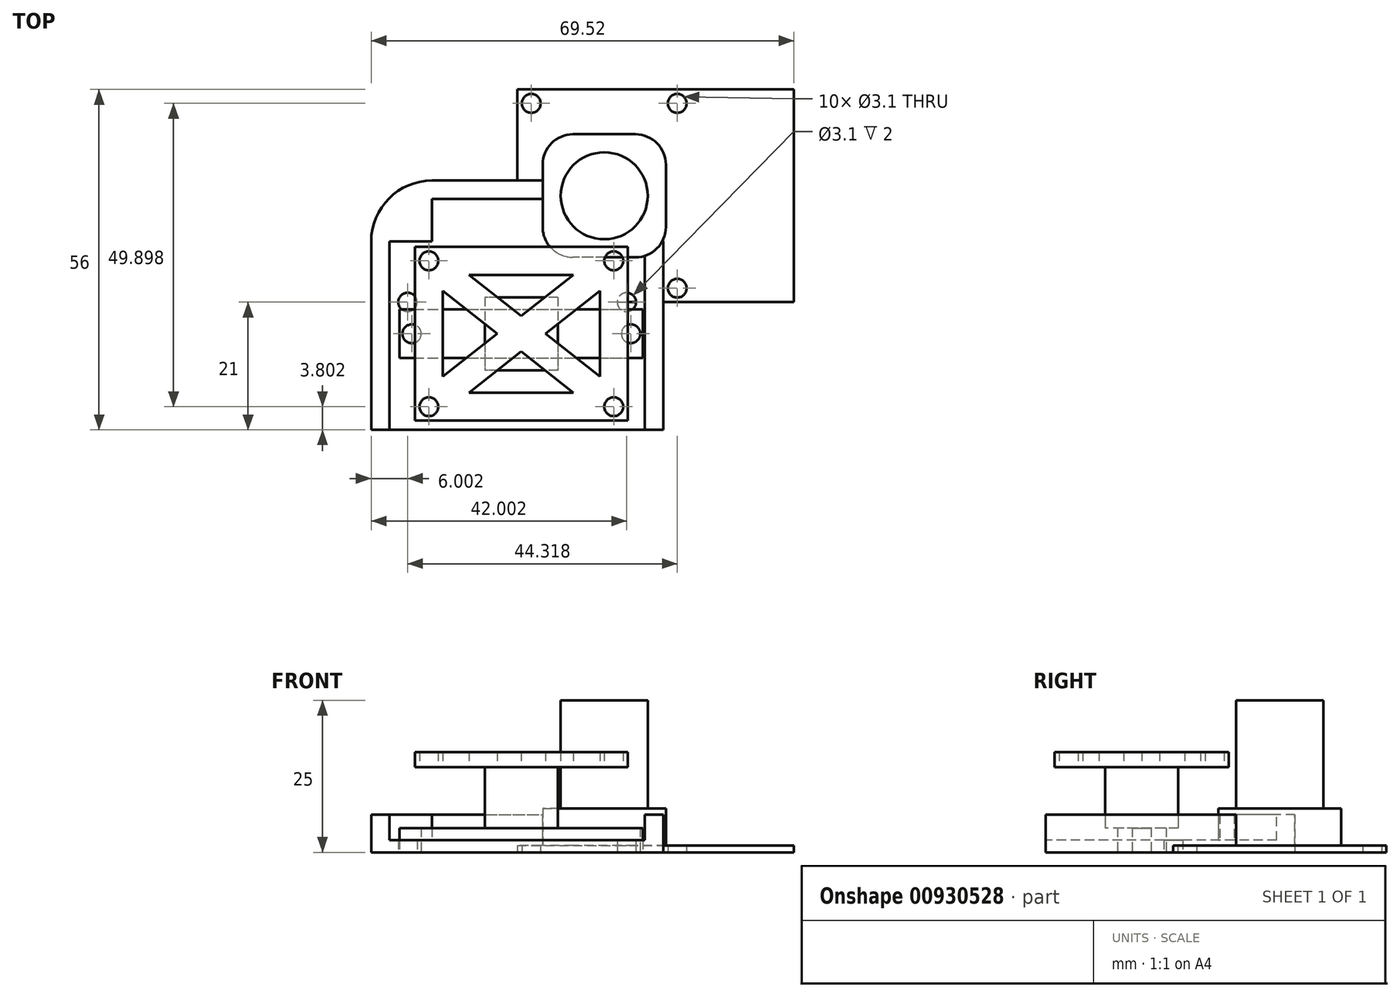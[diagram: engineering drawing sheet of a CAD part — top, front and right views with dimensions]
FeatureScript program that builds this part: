
annotation { "Feature Type Name" : "Feature", "Feature Type Description" : "" }
export const myFeature = defineFeature(function(context is Context, id is Id, definition is map)
    precondition{}
    {
        {
            var Q0;
            Q0=qCreatedBy(makeId("Top.planeOp"),FACE);
            var sketch = newSketch(context, id + "F0", { "sketchPlane" : qUnion([Q0])});
            skLineSegment(sketch, "E0.bottom", {"start": v(0, 0) * mm, "end": v(45.5, 0) * mm});
            skLineSegment(sketch, "E0.top", {"start": v(0, 35) * mm, "end": v(45.5, 35) * mm});
            skLineSegment(sketch, "E0.left", {"start": v(0, 0) * mm, "end": v(0, 35) * mm});
            skLineSegment(sketch, "E0.right", {"start": v(45.5, 0) * mm, "end": v(45.5, 35) * mm});
            skPoint(sketch, "E1", {"position": v(2.3, 32.7) * mm});
            skPoint(sketch, "E2", {"position": v(2.3, 2.3) * mm});
            skPoint(sketch, "E3", {"position": v(26.3, 2.3) * mm});
            skPoint(sketch, "E4", {"position": v(26.3, 32.7) * mm});
            skCircle(sketch, "E5", {"center": v(2.3, 32.7) * mm, "radius": 1.55 * mm});
            skCircle(sketch, "E6", {"center": v(26.3, 32.7) * mm, "radius": 1.55 * mm});
            skCircle(sketch, "E7", {"center": v(26.3, 2.3) * mm, "radius": 1.55 * mm});
            skCircle(sketch, "E8", {"center": v(2.3, 2.3) * mm, "radius": 1.55 * mm});
            skPoint(sketch, "E9", {"position": v(0, 17.5) * mm});
            skPoint(sketch, "E10", {"position": v(22.75, 35) * mm});
            skPoint(sketch, "E11", {"position": v(14.3, 17.5) * mm});
            skLineSegment(sketch, "E12", {"start": v(2.3, 32.7) * mm, "end": v(26.3, 32.7) * mm, "construction": true});
            skLineSegment(sketch, "E13", {"start": v(2.3, 32.7) * mm, "end": v(2.3, 2.3) * mm, "construction": true});
            skPoint(sketch, "E14", {"position": v(14.3, 32.7) * mm});
            skPoint(sketch, "E15", {"position": v(2.3, 17.5) * mm});
            skLineSegment(sketch, "E16.bottom", {"start": v(19.42, 27.63) * mm, "end": v(9.17, 27.63) * mm});
            skLineSegment(sketch, "E16.top", {"start": v(19.42, 7.38) * mm, "end": v(9.18, 7.38) * mm});
            skLineSegment(sketch, "E16.left", {"start": v(24.43, 22.62) * mm, "end": v(24.43, 12.38) * mm});
            skLineSegment(sketch, "E16.right", {"start": v(4.17, 22.62) * mm, "end": v(4.17, 12.38) * mm});
            skPoint(sketch, "E17.visualSharp", {"position": v(4.17, 27.63) * mm});
            skArc(sketch, "E17.filletArc", {"start": v(9.17, 27.63) * mm, "mid": v(5.64, 26.16) * mm, "end": v(4.17, 22.62) * mm});
            skPoint(sketch, "E18.visualSharp", {"position": v(4.18, 7.38) * mm});
            skArc(sketch, "E18.filletArc", {"start": v(4.17, 12.38) * mm, "mid": v(5.64, 8.84) * mm, "end": v(9.18, 7.38) * mm});
            skPoint(sketch, "E19.visualSharp", {"position": v(24.42, 27.63) * mm});
            skArc(sketch, "E19.filletArc", {"start": v(24.43, 22.62) * mm, "mid": v(22.96, 26.16) * mm, "end": v(19.42, 27.63) * mm});
            skPoint(sketch, "E20.visualSharp", {"position": v(24.43, 7.38) * mm});
            skArc(sketch, "E20.filletArc", {"start": v(19.42, 7.38) * mm, "mid": v(22.96, 8.84) * mm, "end": v(24.42, 12.38) * mm});
            skCircle(sketch, "E21", {"center": v(14.3, 17.5) * mm, "radius": 7.15 * mm});
            skSolve(sketch);
        }
        {
            var Q0;
            Q0=makeQuery(id+"F0.imprint","IMPRINT",FACE,{"disambiguationData":[TD([[makeQuery(id+"F0.imprint","IMPRINT",EDGE,{"derivedFrom":sQuery(id+"F0.wireOp",EDGE,"E0.bottom")}),1.0]])]});
            extrude(context, id + "F1", {"entities" : qUnion([Q0]), "depth" : 1.1 * mm, "offsetDistance" : 25 * mm});
        }
        {
            var Q0;
            Q0=makeQuery(id+"F0.imprint","IMPRINT",FACE,{"disambiguationData":[TD([[makeQuery(id+"F0.imprint","IMPRINT",EDGE,{"derivedFrom":sQuery(id+"F0.wireOp",EDGE,"E16.bottom")}),1.0]])]});
            extrude(context, id + "F2", {"entities" : qUnion([Q0]), "operationType" : NewBodyOperationType.ADD, "depth" : 7.2 * mm, "offsetDistance" : 25 * mm});
        }
        {
            var Q0;
            Q0=makeQuery(id+"F0.imprint","IMPRINT",FACE,{"disambiguationData":[TD([[makeQuery(id+"F0.imprint","IMPRINT",EDGE,{"derivedFrom":sQuery(id+"F0.wireOp",EDGE,"E21")}),1.0]])]});
            extrude(context, id + "F3", {"entities" : qUnion([Q0]), "operationType" : NewBodyOperationType.ADD, "depth" : 25 * mm, "offsetDistance" : 25 * mm});
        }
        {
            var Q0;
            Q0=qCreatedBy(makeId("Top.planeOp"),FACE);
            var sketch = newSketch(context, id + "F4", { "sketchPlane" : qUnion([Q0])});
            skLineSegment(sketch, "E22.bottom", {"start": v(-14.02, 20) * mm, "end": v(13.98, 20) * mm});
            skLineSegment(sketch, "E22.top", {"start": v(-24.02, -21) * mm, "end": v(23.98, -21) * mm});
            skLineSegment(sketch, "E22.left", {"start": v(-24.02, 10) * mm, "end": v(-24.02, -21) * mm});
            skLineSegment(sketch, "E22.right", {"start": v(23.98, 10) * mm, "end": v(23.98, -21) * mm});
            skPoint(sketch, "E23.visualSharp", {"position": v(-24.02, 20) * mm});
            skArc(sketch, "E23.filletArc", {"start": v(-14.02, 20) * mm, "mid": v(-21.09, 17.07) * mm, "end": v(-24.02, 10) * mm});
            skPoint(sketch, "E24.visualSharp", {"position": v(23.98, 20) * mm});
            skArc(sketch, "E24.filletArc", {"start": v(23.98, 10) * mm, "mid": v(21.05, 17.07) * mm, "end": v(13.98, 20) * mm});
            skLineSegment(sketch, "E25.0", {"start": v(-21.02, 10) * mm, "end": v(-21.02, -21) * mm});
            skLineSegment(sketch, "E25.1", {"start": v(20.98, 10) * mm, "end": v(20.98, -21) * mm});
            skArc(sketch, "E25.2", {"start": v(20.98, 10) * mm, "mid": v(18.93, 14.95) * mm, "end": v(13.98, 17) * mm});
            skLineSegment(sketch, "E25.3", {"start": v(-14.02, 17) * mm, "end": v(13.98, 17) * mm});
            skArc(sketch, "E25.4", {"start": v(-14.02, 17) * mm, "mid": v(-18.97, 14.95) * mm, "end": v(-21.02, 10) * mm});
            skPoint(sketch, "E26", {"position": v(17.98, 0) * mm});
            skPoint(sketch, "E27", {"position": v(-18.02, 0) * mm});
            skCircle(sketch, "E28", {"center": v(-18.02, 0) * mm, "radius": 1.55 * mm});
            skCircle(sketch, "E29", {"center": v(17.98, 0) * mm, "radius": 1.55 * mm});
            skLineSegment(sketch, "E30", {"start": v(-21.02, 10) * mm, "end": v(-14.02, 10) * mm});
            skLineSegment(sketch, "E31", {"start": v(-14.02, 17) * mm, "end": v(-14.02, 10) * mm});
            skLineSegment(sketch, "E32", {"start": v(13.98, 17) * mm, "end": v(13.98, 10) * mm});
            skLineSegment(sketch, "E33", {"start": v(20.98, 10) * mm, "end": v(13.98, 10) * mm});
            skSolve(sketch);
        }
        {
            var Q0;
            {var subQ1=sQuery(id+"F4.wireOp",EDGE,"E25.0");Q0=makeQuery(id+"F4.imprint","IMPRINT",FACE,{"disambiguationData":[TD([[makeQuery(id+"F4.imprint","IMPRINT",EDGE,{"derivedFrom":subQ1}),1.0]])]});}
            extrude(context, id + "F5", {"entities" : qUnion([Q0]), "depth" : 2 * mm, "offsetDistance" : 25 * mm});
        }
        {
            var Q0;
            Q0=makeQuery(id+"F4.imprint","IMPRINT",FACE,{"disambiguationData":[TD([[makeQuery(id+"F4.imprint","IMPRINT",EDGE,{"derivedFrom":sQuery(id+"F4.wireOp",EDGE,"E22.bottom")}),-1.0]])]});
            var Q1;
            Q1=makeQuery(id+"F4.imprint","IMPRINT",FACE,{"disambiguationData":[TD([[makeQuery(id+"F4.imprint","IMPRINT",EDGE,{"derivedFrom":sQuery(id+"F4.wireOp",EDGE,"E25.2")}),1.0]])]});
            var Q2;
            Q2=makeQuery(id+"F4.imprint","IMPRINT",FACE,{"disambiguationData":[TD([[makeQuery(id+"F4.imprint","IMPRINT",EDGE,{"derivedFrom":sQuery(id+"F4.wireOp",EDGE,"E25.4")}),1.0]])]});
            extrude(context, id + "F6", {"entities" : qUnion([Q0, Q1, Q2]), "operationType" : NewBodyOperationType.ADD, "depth" : 6.17 * mm, "offsetDistance" : 25 * mm});
        }
        {
            var Q0;
            Q0=qCreatedBy(makeId("Top.planeOp"),FACE);
            var sketch = newSketch(context, id + "F7", { "sketchPlane" : qUnion([Q0])});
            skLineSegment(sketch, "E34.bottom", {"start": v(-19.33, -1.2) * mm, "end": v(20.67, -1.2) * mm});
            skLineSegment(sketch, "E34.top", {"start": v(-19.33, -9.2) * mm, "end": v(20.67, -9.2) * mm});
            skLineSegment(sketch, "E34.left", {"start": v(-19.33, -1.2) * mm, "end": v(-19.33, -9.2) * mm});
            skLineSegment(sketch, "E34.right", {"start": v(20.67, -1.2) * mm, "end": v(20.67, -9.2) * mm});
            skPoint(sketch, "E35", {"position": v(0.67, -1.2) * mm});
            skPoint(sketch, "E36", {"position": v(-19.33, -5.2) * mm});
            skPoint(sketch, "E37", {"position": v(-17.33, -5.2) * mm});
            skPoint(sketch, "E38", {"position": v(18.67, -5.2) * mm});
            skCircle(sketch, "E39", {"center": v(-17.33, -5.2) * mm, "radius": 1.55 * mm});
            skCircle(sketch, "E40", {"center": v(18.67, -5.2) * mm, "radius": 1.55 * mm});
            skSolve(sketch);
        }
        {
            var Q0;
            Q0=makeQuery(id+"F7.imprint","IMPRINT",FACE,{"disambiguationData":[TD([[makeQuery(id+"F7.imprint","IMPRINT",EDGE,{"derivedFrom":sQuery(id+"F7.wireOp",EDGE,"E34.bottom")}),-1.0]])]});
            extrude(context, id + "F8", {"entities" : qUnion([Q0]), "depth" : 4 * mm, "offsetDistance" : 25 * mm});
        }
        {
            var Q0;
            Q0=makeQuery(id+"F8.opExtrude","CAP_FACE",FACE,{"disambiguationData":[OSD([sQuery(id+"F7.wireOp",EDGE,"E34.bottom"),sQuery(id+"F7.wireOp",EDGE,"E34.top"),sQuery(id+"F7.wireOp",EDGE,"E34.left"),sQuery(id+"F7.wireOp",EDGE,"E34.right"),sQuery(id+"F7.wireOp",EDGE,"E39"),sQuery(id+"F7.wireOp",EDGE,"E40")])],"isStart":false});
            var sketch = newSketch(context, id + "F9", { "sketchPlane" : qUnion([Q0])});
            skPoint(sketch, "E41", {"position": v(0.67, -1.2) * mm});
            skPoint(sketch, "E42", {"position": v(-19.33, -5.2) * mm});
            skPoint(sketch, "E43", {"position": v(-17.33, -5.2) * mm});
            skPoint(sketch, "E44", {"position": v(18.67, -5.2) * mm});
            skPoint(sketch, "E45", {"position": v(0.67, -5.2) * mm});
            skLineSegment(sketch, "E46.bottom", {"start": v(6.67, 0.8) * mm, "end": v(-5.33, 0.8) * mm});
            skLineSegment(sketch, "E46.top", {"start": v(6.67, -11.2) * mm, "end": v(-5.33, -11.2) * mm});
            skLineSegment(sketch, "E46.left", {"start": v(6.67, 0.8) * mm, "end": v(6.67, -11.2) * mm});
            skLineSegment(sketch, "E46.right", {"start": v(-5.33, 0.8) * mm, "end": v(-5.33, -11.2) * mm});
            skSolve(sketch);
        }
        {
            var Q0;
            {var subQ0=sQuery(id+"F9.wireOp",EDGE,"E46.bottom");Q0=makeQuery(id+"F9.imprint","IMPRINT",FACE,{"disambiguationData":[TD([[makeQuery(id+"F9.imprint","IMPRINT",EDGE,{"derivedFrom":subQ0}),1.0]])]});}
            var Q1;
            {var subQ0=sQuery(id+"F9.wireOp",EDGE,"E46.top");Q1=makeQuery(id+"F9.imprint","IMPRINT",FACE,{"disambiguationData":[TD([[makeQuery(id+"F9.imprint","IMPRINT",EDGE,{"derivedFrom":subQ0}),-1.0]])]});}
            var Q2;
            {var subQ0=sQuery(id+"F9.wireOp",EDGE,"E46.left");var subQ1=makeQuery(id+"F8.opExtrude","CAP_EDGE",EDGE,{"disambiguationData":[OSD([sQuery(id+"F7.wireOp",EDGE,"E34.bottom")])],"isStart":false});var subQ2=makeQuery(id+"F9.imprint","INTERSECT",VERTEX,{"derivedFrom":[subQ1,subQ0]});Q2=makeQuery(id+"F9.imprint","IMPRINT",FACE,{"disambiguationData":[TD([[makeQuery(id+"F9.imprint","IMPRINT",EDGE,{"disambiguationData":[TD([[subQ2,-1.0]])],"derivedFrom":subQ0}),-1.0]])]});}
            extrude(context, id + "F10", {"entities" : qUnion([Q0, Q1, Q2]), "depth" : 10 * mm, "offsetDistance" : 25 * mm});
        }
        {
            var Q0;
            Q0=makeQuery(id+"F10.opExtrude","CAP_FACE",FACE,{"disambiguationData":[OSD([sQuery(id+"F9.wireOp",EDGE,"E46.bottom"),sQuery(id+"F9.wireOp",EDGE,"E46.top"),sQuery(id+"F9.wireOp",EDGE,"E46.left"),sQuery(id+"F9.wireOp",EDGE,"E46.right")])],"isStart":false});
            var sketch = newSketch(context, id + "F11", { "sketchPlane" : qUnion([Q0])});
            skPoint(sketch, "E47", {"position": v(0.67, 0.8) * mm});
            skPoint(sketch, "E48", {"position": v(-5.33, -5.2) * mm});
            skPoint(sketch, "E49", {"position": v(0.67, -5.2) * mm});
            skLineSegment(sketch, "E50.bottom", {"start": v(18.17, 9.1) * mm, "end": v(-16.83, 9.1) * mm});
            skLineSegment(sketch, "E50.top", {"start": v(18.17, -19.5) * mm, "end": v(-16.83, -19.5) * mm});
            skLineSegment(sketch, "E50.left", {"start": v(18.17, 9.1) * mm, "end": v(18.17, -19.5) * mm});
            skLineSegment(sketch, "E50.right", {"start": v(-16.83, 9.1) * mm, "end": v(-16.83, -19.5) * mm});
            skLineSegment(sketch, "E51.0", {"start": v(-12.23, 4.5) * mm, "end": v(-12.23, -14.9) * mm});
            skLineSegment(sketch, "E51.1", {"start": v(13.57, 4.5) * mm, "end": v(-12.23, 4.5) * mm});
            skLineSegment(sketch, "E51.2", {"start": v(13.57, 4.5) * mm, "end": v(13.57, -14.9) * mm});
            skLineSegment(sketch, "E51.3", {"start": v(13.57, -14.9) * mm, "end": v(-12.23, -14.9) * mm});
            skLineSegment(sketch, "E52", {"start": v(-12.23, 4.5) * mm, "end": v(-16.83, 4.5) * mm, "construction": true});
            skLineSegment(sketch, "E53", {"start": v(-12.23, 4.5) * mm, "end": v(-12.23, 9.1) * mm, "construction": true});
            skLineSegment(sketch, "E54", {"start": v(13.57, 4.5) * mm, "end": v(13.57, 9.1) * mm, "construction": true});
            skLineSegment(sketch, "E55", {"start": v(13.57, 4.5) * mm, "end": v(18.17, 4.5) * mm, "construction": true});
            skPoint(sketch, "E56", {"position": v(-14.53, 6.8) * mm});
            skPoint(sketch, "E56.positionSnap0", {"position": v(-14.53, 4.5) * mm});
            skPoint(sketch, "E56.positionSnap1", {"position": v(-12.23, 6.8) * mm});
            skPoint(sketch, "E57", {"position": v(15.87, 6.8) * mm});
            skPoint(sketch, "E57.positionSnap0", {"position": v(13.57, 6.8) * mm});
            skPoint(sketch, "E57.positionSnap1", {"position": v(15.87, 4.5) * mm});
            skLineSegment(sketch, "E58", {"start": v(-14.53, 6.8) * mm, "end": v(0.67, -5.2) * mm});
            skLineSegment(sketch, "E59", {"start": v(15.87, 6.8) * mm, "end": v(0.67, -5.2) * mm});
            skLineSegment(sketch, "E60", {"start": v(-14.53, 6.8) * mm, "end": v(-13.1, 8.6) * mm});
            skLineSegment(sketch, "E61", {"start": v(-13.1, 8.6) * mm, "end": v(0.67, -2.27) * mm});
            skLineSegment(sketch, "E62", {"start": v(0.67, -2.27) * mm, "end": v(14.44, 8.6) * mm});
            skLineSegment(sketch, "E63", {"start": v(14.44, 8.6) * mm, "end": v(15.87, 6.8) * mm});
            skLineSegment(sketch, "E64", {"start": v(-12.23, -14.9) * mm, "end": v(-12.23, -19.5) * mm, "construction": true});
            skLineSegment(sketch, "E65", {"start": v(-12.23, -19.5) * mm, "end": v(-12.23, -14.9) * mm, "construction": true});
            skLineSegment(sketch, "E66", {"start": v(-16.83, -14.9) * mm, "end": v(-12.23, -14.9) * mm, "construction": true});
            skLineSegment(sketch, "E67", {"start": v(13.57, -14.9) * mm, "end": v(18.17, -14.9) * mm, "construction": true});
            skLineSegment(sketch, "E68", {"start": v(18.17, -14.9) * mm, "end": v(13.57, -14.9) * mm, "construction": true});
            skLineSegment(sketch, "E69", {"start": v(13.57, -14.9) * mm, "end": v(13.57, -19.5) * mm, "construction": true});
            skLineSegment(sketch, "E70", {"start": v(13.57, -19.5) * mm, "end": v(13.57, -14.9) * mm, "construction": true});
            skPoint(sketch, "E71", {"position": v(-14.53, -17.2) * mm});
            skPoint(sketch, "E71.positionSnap0", {"position": v(-12.23, -17.2) * mm});
            skPoint(sketch, "E71.positionSnap1", {"position": v(-14.53, -14.9) * mm});
            skPoint(sketch, "E72", {"position": v(15.87, -17.2) * mm});
            skPoint(sketch, "E72.positionSnap0", {"position": v(13.57, -17.2) * mm});
            skPoint(sketch, "E72.positionSnap1", {"position": v(15.87, -14.9) * mm});
            skLineSegment(sketch, "E73", {"start": v(-14.53, -17.2) * mm, "end": v(0.67, -5.2) * mm});
            skLineSegment(sketch, "E74", {"start": v(15.87, -17.2) * mm, "end": v(0.67, -5.2) * mm});
            skLineSegment(sketch, "E75", {"start": v(-14.53, 6.8) * mm, "end": v(-16.05, 4.87) * mm});
            skLineSegment(sketch, "E76", {"start": v(-5.33, -5.2) * mm, "end": v(0.67, -5.2) * mm, "construction": true});
            skLineSegment(sketch, "E77", {"start": v(-16.05, 4.87) * mm, "end": v(-3.3, -5.2) * mm});
            skLineSegment(sketch, "E78", {"start": v(-16.83, -5.2) * mm, "end": v(18.17, -5.2) * mm, "construction": true});
            skLineSegment(sketch, "E79", {"start": v(0.67, 9.1) * mm, "end": v(0.67, -19.5) * mm, "construction": true});
            skLineSegment(sketch, "E80.MirrorCS", {"start": v(-16.05, -15.27) * mm, "end": v(-3.3, -5.2) * mm});
            skLineSegment(sketch, "E81.MirrorCS", {"start": v(-14.53, -17.2) * mm, "end": v(-16.05, -15.27) * mm});
            skLineSegment(sketch, "E82.MirrorCS", {"start": v(-14.53, -17.2) * mm, "end": v(-13.1, -19) * mm});
            skLineSegment(sketch, "E83.MirrorCS", {"start": v(-13.1, -19) * mm, "end": v(0.67, -8.13) * mm});
            skLineSegment(sketch, "E84.MirrorCS", {"start": v(15.87, 6.8) * mm, "end": v(17.4, 4.87) * mm});
            skLineSegment(sketch, "E85.MirrorCS", {"start": v(17.4, 4.87) * mm, "end": v(4.63, -5.2) * mm});
            skLineSegment(sketch, "E86.MirrorCS", {"start": v(17.4, -15.27) * mm, "end": v(4.63, -5.2) * mm});
            skLineSegment(sketch, "E87.MirrorCS", {"start": v(15.87, -17.2) * mm, "end": v(17.4, -15.27) * mm});
            skLineSegment(sketch, "E88.MirrorCS", {"start": v(15.87, -17.2) * mm, "end": v(14.44, -19) * mm});
            skLineSegment(sketch, "E89.MirrorCS", {"start": v(14.44, -19) * mm, "end": v(0.67, -8.13) * mm});
            skCircle(sketch, "E90", {"center": v(-14.53, 6.8) * mm, "radius": 1.55 * mm});
            skCircle(sketch, "E91", {"center": v(15.87, 6.8) * mm, "radius": 1.55 * mm});
            skCircle(sketch, "E92", {"center": v(15.87, -17.2) * mm, "radius": 1.55 * mm});
            skCircle(sketch, "E93", {"center": v(-14.53, -17.2) * mm, "radius": 1.55 * mm});
            skSolve(sketch);
        }
        {
            var Q0;
            Q0=makeQuery(id+"F11.imprint","IMPRINT",FACE,{"disambiguationData":[TD([[makeQuery(id+"F11.imprint","IMPRINT",EDGE,{"derivedFrom":sQuery(id+"F11.wireOp",EDGE,"E50.bottom")}),1.0]])]});
            var Q1;
            {var subQ1=sQuery(id+"F11.wireOp",EDGE,"E51.1");var subQ7=sQuery(id+"F11.wireOp",EDGE,"E59");var subQ8=makeQuery(id+"F11.imprint","INTERSECT",VERTEX,{"derivedFrom":[subQ1,subQ7]});Q1=makeQuery(id+"F11.imprint","IMPRINT",FACE,{"disambiguationData":[TD([[makeQuery(id+"F11.imprint","IMPRINT",EDGE,{"disambiguationData":[TD([[subQ8,-1.0]])],"derivedFrom":subQ1}),1.0]])]});}
            var Q2;
            {var subQ1=sQuery(id+"F11.wireOp",EDGE,"E51.2");var subQ6=sQuery(id+"F11.wireOp",EDGE,"E51.1");var subQ9=makeQuery(id+"F11.imprint","INTERSECT",VERTEX,{"derivedFrom":[subQ6,subQ1]});Q2=makeQuery(id+"F11.imprint","IMPRINT",FACE,{"disambiguationData":[TD([[makeQuery(id+"F11.imprint","IMPRINT",EDGE,{"disambiguationData":[TD([[subQ9,-1.0]])],"derivedFrom":subQ6}),1.0]])]});}
            var Q3;
            {var subQ0=sQuery(id+"F11.wireOp",EDGE,"E62");var subQ1=sQuery(id+"F11.wireOp",EDGE,"E61");var subQ2=makeQuery(id+"F11.imprint","INTERSECT",VERTEX,{"derivedFrom":[subQ1,subQ0]});Q3=makeQuery(id+"F11.imprint","IMPRINT",FACE,{"disambiguationData":[TD([[makeQuery(id+"F11.imprint","IMPRINT",EDGE,{"disambiguationData":[TD([[subQ2,1.0]])],"derivedFrom":subQ1}),-1.0]])]});}
            var Q4;
            {var subQ0=sQuery(id+"F11.wireOp",EDGE,"E86.MirrorCS");var subQ1=sQuery(id+"F11.wireOp",EDGE,"E85.MirrorCS");var subQ2=makeQuery(id+"F11.imprint","INTERSECT",VERTEX,{"derivedFrom":[subQ1,subQ0]});Q4=makeQuery(id+"F11.imprint","IMPRINT",FACE,{"disambiguationData":[TD([[makeQuery(id+"F11.imprint","IMPRINT",EDGE,{"disambiguationData":[TD([[subQ2,1.0]])],"derivedFrom":subQ1}),-1.0]])]});}
            var Q5;
            {var subQ0=sQuery(id+"F11.wireOp",EDGE,"E61");var subQ1=sQuery(id+"F11.wireOp",EDGE,"E51.1");var subQ2=makeQuery(id+"F11.imprint","INTERSECT",VERTEX,{"derivedFrom":[subQ1,subQ0]});Q5=makeQuery(id+"F11.imprint","IMPRINT",FACE,{"disambiguationData":[TD([[makeQuery(id+"F11.imprint","IMPRINT",EDGE,{"disambiguationData":[TD([[subQ2,-1.0]])],"derivedFrom":subQ1}),1.0]])]});}
            var Q6;
            {var subQ1=sQuery(id+"F11.wireOp",EDGE,"E51.0");var subQ6=sQuery(id+"F11.wireOp",EDGE,"E51.1");var subQ9=makeQuery(id+"F11.imprint","INTERSECT",VERTEX,{"derivedFrom":[subQ1,subQ6]});Q6=makeQuery(id+"F11.imprint","IMPRINT",FACE,{"disambiguationData":[TD([[makeQuery(id+"F11.imprint","IMPRINT",EDGE,{"disambiguationData":[TD([[subQ9,-1.0]])],"derivedFrom":subQ1}),1.0]])]});}
            var Q7;
            {var subQ1=sQuery(id+"F11.wireOp",EDGE,"E51.0");var subQ7=sQuery(id+"F11.wireOp",EDGE,"E51.3");var subQ9=makeQuery(id+"F11.imprint","INTERSECT",VERTEX,{"derivedFrom":[subQ1,subQ7]});Q7=makeQuery(id+"F11.imprint","IMPRINT",FACE,{"disambiguationData":[TD([[makeQuery(id+"F11.imprint","IMPRINT",EDGE,{"disambiguationData":[TD([[subQ9,1.0]])],"derivedFrom":subQ1}),1.0]])]});}
            var Q8;
            {var subQ0=sQuery(id+"F11.wireOp",EDGE,"E83.MirrorCS");var subQ1=sQuery(id+"F11.wireOp",EDGE,"E51.3");var subQ2=makeQuery(id+"F11.imprint","INTERSECT",VERTEX,{"derivedFrom":[subQ1,subQ0]});Q8=makeQuery(id+"F11.imprint","IMPRINT",FACE,{"disambiguationData":[TD([[makeQuery(id+"F11.imprint","IMPRINT",EDGE,{"disambiguationData":[TD([[subQ2,-1.0]])],"derivedFrom":subQ1}),-1.0]])]});}
            var Q9;
            {var subQ0=sQuery(id+"F11.wireOp",EDGE,"E89.MirrorCS");var subQ1=sQuery(id+"F11.wireOp",EDGE,"E83.MirrorCS");var subQ2=makeQuery(id+"F11.imprint","INTERSECT",VERTEX,{"derivedFrom":[subQ1,subQ0]});Q9=makeQuery(id+"F11.imprint","IMPRINT",FACE,{"disambiguationData":[TD([[makeQuery(id+"F11.imprint","IMPRINT",EDGE,{"disambiguationData":[TD([[subQ2,1.0]])],"derivedFrom":subQ1}),1.0]])]});}
            var Q10;
            {var subQ0=sQuery(id+"F11.wireOp",EDGE,"E80.MirrorCS");var subQ1=sQuery(id+"F11.wireOp",EDGE,"E77");var subQ2=makeQuery(id+"F11.imprint","INTERSECT",VERTEX,{"derivedFrom":[subQ1,subQ0]});Q10=makeQuery(id+"F11.imprint","IMPRINT",FACE,{"disambiguationData":[TD([[makeQuery(id+"F11.imprint","IMPRINT",EDGE,{"disambiguationData":[TD([[subQ2,1.0]])],"derivedFrom":subQ1}),1.0]])]});}
            var Q11;
            {var subQ5=sQuery(id+"F11.wireOp",EDGE,"E51.3");var subQ7=sQuery(id+"F11.wireOp",EDGE,"E74");var subQ8=makeQuery(id+"F11.imprint","INTERSECT",VERTEX,{"derivedFrom":[subQ5,subQ7]});Q11=makeQuery(id+"F11.imprint","IMPRINT",FACE,{"disambiguationData":[TD([[makeQuery(id+"F11.imprint","IMPRINT",EDGE,{"disambiguationData":[TD([[subQ8,-1.0]])],"derivedFrom":subQ5}),-1.0]])]});}
            var Q12;
            {var subQ1=sQuery(id+"F11.wireOp",EDGE,"E51.2");var subQ6=sQuery(id+"F11.wireOp",EDGE,"E51.3");var subQ9=makeQuery(id+"F11.imprint","INTERSECT",VERTEX,{"derivedFrom":[subQ1,subQ6]});Q12=makeQuery(id+"F11.imprint","IMPRINT",FACE,{"disambiguationData":[TD([[makeQuery(id+"F11.imprint","IMPRINT",EDGE,{"disambiguationData":[TD([[subQ9,1.0]])],"derivedFrom":subQ1}),-1.0]])]});}
            var Q13;
            {var subQ6=sQuery(id+"F11.wireOp",EDGE,"E51.1");var subQ9=sQuery(id+"F11.wireOp",EDGE,"E51.0");var subQ10=makeQuery(id+"F11.imprint","INTERSECT",VERTEX,{"derivedFrom":[subQ9,subQ6]});Q13=makeQuery(id+"F11.imprint","IMPRINT",FACE,{"disambiguationData":[TD([[makeQuery(id+"F11.imprint","IMPRINT",EDGE,{"disambiguationData":[TD([[subQ10,-1.0]])],"derivedFrom":subQ9}),-1.0]])]});}
            var Q14;
            {var subQ0=sQuery(id+"F11.wireOp",EDGE,"E61");var subQ6=sQuery(id+"F11.wireOp",EDGE,"E51.1");var subQ9=makeQuery(id+"F11.imprint","INTERSECT",VERTEX,{"derivedFrom":[subQ6,subQ0]});Q14=makeQuery(id+"F11.imprint","IMPRINT",FACE,{"disambiguationData":[TD([[makeQuery(id+"F11.imprint","IMPRINT",EDGE,{"disambiguationData":[TD([[subQ9,-1.0]])],"derivedFrom":subQ6}),-1.0]])]});}
            var Q15;
            {var subQ1=sQuery(id+"F11.wireOp",EDGE,"E51.3");var subQ5=sQuery(id+"F11.wireOp",EDGE,"E51.0");var subQ6=makeQuery(id+"F11.imprint","INTERSECT",VERTEX,{"derivedFrom":[subQ5,subQ1]});Q15=makeQuery(id+"F11.imprint","IMPRINT",FACE,{"disambiguationData":[TD([[makeQuery(id+"F11.imprint","IMPRINT",EDGE,{"disambiguationData":[TD([[subQ6,1.0]])],"derivedFrom":subQ5}),-1.0]])]});}
            var Q16;
            {var subQ0=sQuery(id+"F11.wireOp",EDGE,"E83.MirrorCS");var subQ6=sQuery(id+"F11.wireOp",EDGE,"E51.3");var subQ9=makeQuery(id+"F11.imprint","INTERSECT",VERTEX,{"derivedFrom":[subQ6,subQ0]});Q16=makeQuery(id+"F11.imprint","IMPRINT",FACE,{"disambiguationData":[TD([[makeQuery(id+"F11.imprint","IMPRINT",EDGE,{"disambiguationData":[TD([[subQ9,-1.0]])],"derivedFrom":subQ6}),1.0]])]});}
            var Q17;
            {var subQ5=sQuery(id+"F11.wireOp",EDGE,"E74");var subQ7=sQuery(id+"F11.wireOp",EDGE,"E51.3");var subQ9=makeQuery(id+"F11.imprint","INTERSECT",VERTEX,{"derivedFrom":[subQ7,subQ5]});Q17=makeQuery(id+"F11.imprint","IMPRINT",FACE,{"disambiguationData":[TD([[makeQuery(id+"F11.imprint","IMPRINT",EDGE,{"disambiguationData":[TD([[subQ9,-1.0]])],"derivedFrom":subQ7}),1.0]])]});}
            var Q18;
            {var subQ3=sQuery(id+"F11.wireOp",EDGE,"E51.2");var subQ6=sQuery(id+"F11.wireOp",EDGE,"E51.3");var subQ10=makeQuery(id+"F11.imprint","INTERSECT",VERTEX,{"derivedFrom":[subQ3,subQ6]});Q18=makeQuery(id+"F11.imprint","IMPRINT",FACE,{"disambiguationData":[TD([[makeQuery(id+"F11.imprint","IMPRINT",EDGE,{"disambiguationData":[TD([[subQ10,1.0]])],"derivedFrom":subQ3}),1.0]])]});}
            var Q19;
            {var subQ5=sQuery(id+"F11.wireOp",EDGE,"E59");var subQ6=sQuery(id+"F11.wireOp",EDGE,"E51.1");var subQ7=makeQuery(id+"F11.imprint","INTERSECT",VERTEX,{"derivedFrom":[subQ6,subQ5]});Q19=makeQuery(id+"F11.imprint","IMPRINT",FACE,{"disambiguationData":[TD([[makeQuery(id+"F11.imprint","IMPRINT",EDGE,{"disambiguationData":[TD([[subQ7,-1.0]])],"derivedFrom":subQ6}),-1.0]])]});}
            var Q20;
            {var subQ1=sQuery(id+"F11.wireOp",EDGE,"E51.1");var subQ9=sQuery(id+"F11.wireOp",EDGE,"E51.2");var subQ10=makeQuery(id+"F11.imprint","INTERSECT",VERTEX,{"derivedFrom":[subQ1,subQ9]});Q20=makeQuery(id+"F11.imprint","IMPRINT",FACE,{"disambiguationData":[TD([[makeQuery(id+"F11.imprint","IMPRINT",EDGE,{"disambiguationData":[TD([[subQ10,-1.0]])],"derivedFrom":subQ1}),-1.0]])]});}
            extrude(context, id + "F12", {"entities" : qUnion([Q0, Q1, Q2, Q3, Q4, Q5, Q6, Q7, Q8, Q9, Q10, Q11, Q12, Q13, Q14, Q15, Q16, Q17, Q18, Q19, Q20]), "operationType" : NewBodyOperationType.ADD, "depth" : 2.5 * mm, "offsetDistance" : 25 * mm});
        }
    });
